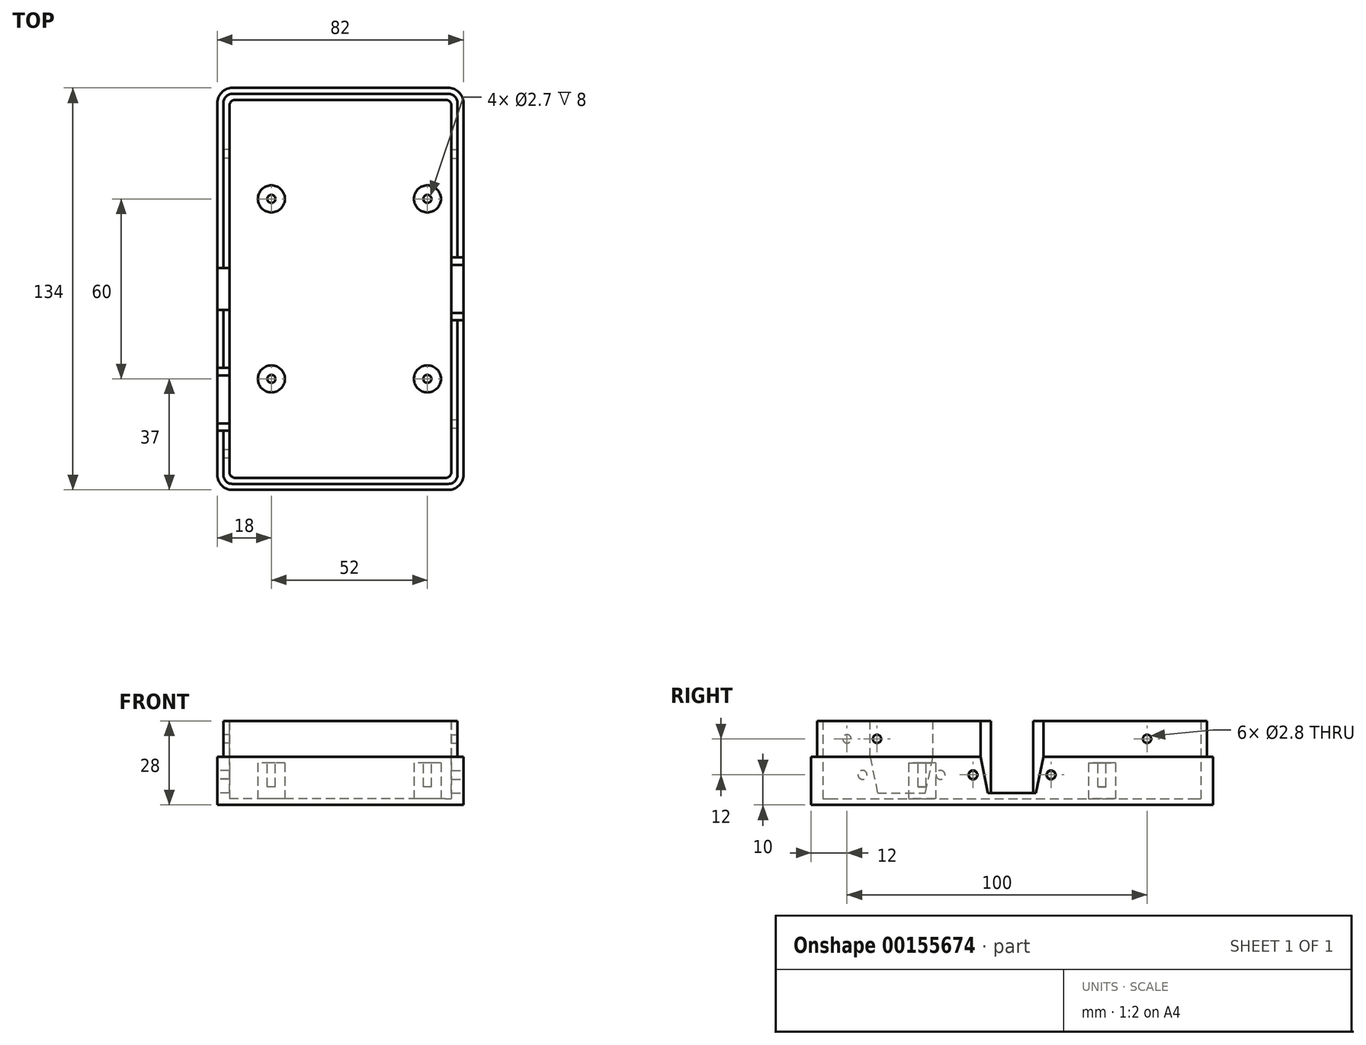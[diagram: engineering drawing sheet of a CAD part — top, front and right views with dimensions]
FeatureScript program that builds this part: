
annotation { "Feature Type Name" : "Feature", "Feature Type Description" : "" }
export const myFeature = defineFeature(function(context is Context, id is Id, definition is map)
    precondition{}
    {
        {
            var Q0;
            Q0=qCreatedBy(makeId("Top.planeOp"),FACE);
            var sketch = newSketch(context, id + "F0", { "sketchPlane" : qUnion([Q0])});
            skLineSegment(sketch, "E0.bottom", {"start": v(36, -67) * mm, "end": v(-36, -67) * mm});
            skLineSegment(sketch, "E0.top", {"start": v(36, 67) * mm, "end": v(-36, 67) * mm});
            skLineSegment(sketch, "E0.left", {"start": v(41, -62) * mm, "end": v(41, 62) * mm});
            skLineSegment(sketch, "E0.right", {"start": v(-41, -62) * mm, "end": v(-41, 62) * mm});
            skPoint(sketch, "E0.middle", {"position": v(0, 0) * mm});
            skPoint(sketch, "E1.visualSharp", {"position": v(-41, 67) * mm});
            skArc(sketch, "E1.filletArc", {"start": v(-36, 67) * mm, "mid": v(-39.54, 65.54) * mm, "end": v(-41, 62) * mm});
            skPoint(sketch, "E2.visualSharp", {"position": v(41, 67) * mm});
            skArc(sketch, "E2.filletArc", {"start": v(41, 62) * mm, "mid": v(39.54, 65.54) * mm, "end": v(36, 67) * mm});
            skPoint(sketch, "E3.visualSharp", {"position": v(41, -67) * mm});
            skArc(sketch, "E3.filletArc", {"start": v(36, -67) * mm, "mid": v(39.54, -65.54) * mm, "end": v(41, -62) * mm});
            skPoint(sketch, "E4.visualSharp", {"position": v(-41, -67) * mm});
            skArc(sketch, "E4.filletArc", {"start": v(-41, -62) * mm, "mid": v(-39.54, -65.54) * mm, "end": v(-36, -67) * mm});
            skSolve(sketch);
        }
        {
            var Q0;
            Q0=qSketchRegion(id+"F0",true);
            extrude(context, id + "F1", {"entities" : qUnion([Q0]), "depth" : 16 * mm});
        }
        {
            var Q0;
            Q0=makeQuery(id+"F1.opExtrude","CAP_FACE",FACE,{"disambiguationData":[OSD([sQuery(id+"F0.wireOp",EDGE,"E0.bottom"),sQuery(id+"F0.wireOp",EDGE,"E0.top"),sQuery(id+"F0.wireOp",EDGE,"E0.left"),sQuery(id+"F0.wireOp",EDGE,"E0.right"),sQuery(id+"F0.wireOp",EDGE,"E1.filletArc"),sQuery(id+"F0.wireOp",EDGE,"E2.filletArc"),sQuery(id+"F0.wireOp",EDGE,"E3.filletArc"),sQuery(id+"F0.wireOp",EDGE,"E4.filletArc")])],"isStart":false});
            shell(context, id + "F2", {"entities" : qUnion([Q0]), "thickness" : 2 * mm});
        }
        {
            var Q0;
            Q0=makeQuery(id+"F2.opShell","OFFSET_FACE",FACE,{"disambiguationData":[OSD([sQuery(id+"F0.wireOp",EDGE,"E0.bottom"),sQuery(id+"F0.wireOp",EDGE,"E0.top"),sQuery(id+"F0.wireOp",EDGE,"E0.left"),sQuery(id+"F0.wireOp",EDGE,"E0.right"),sQuery(id+"F0.wireOp",EDGE,"E1.filletArc"),sQuery(id+"F0.wireOp",EDGE,"E2.filletArc"),sQuery(id+"F0.wireOp",EDGE,"E3.filletArc"),sQuery(id+"F0.wireOp",EDGE,"E4.filletArc")])]});
            var sketch = newSketch(context, id + "F3", { "sketchPlane" : qUnion([Q0])});
            skCircle(sketch, "E5", {"center": v(-23, 30) * mm, "radius": 4.5 * mm});
            skCircle(sketch, "E6", {"center": v(29, 30) * mm, "radius": 4.5 * mm});
            skCircle(sketch, "E7", {"center": v(-23, -30) * mm, "radius": 4.5 * mm});
            skCircle(sketch, "E8", {"center": v(29, -30) * mm, "radius": 4.5 * mm});
            skLineSegment(sketch, "E9.bottom", {"start": v(36, -65) * mm, "end": v(-36, -65) * mm});
            skLineSegment(sketch, "E9.left", {"start": v(39, -62) * mm, "end": v(39, 62) * mm});
            skLineSegment(sketch, "E9.right", {"start": v(-39, -62) * mm, "end": v(-39, 62) * mm});
            skPoint(sketch, "E9.middle", {"position": v(0, 0) * mm});
            skLineSegment(sketch, "E10.bottom", {"start": v(35, -63) * mm, "end": v(-35, -63) * mm});
            skLineSegment(sketch, "E10.left", {"start": v(37, -61) * mm, "end": v(37, 61) * mm});
            skLineSegment(sketch, "E10.right", {"start": v(-37, -61) * mm, "end": v(-37, 61) * mm});
            skPoint(sketch, "E11.visualSharp", {"position": v(-39, -65) * mm});
            skArc(sketch, "E11.filletArc", {"start": v(-39, -62) * mm, "mid": v(-38.12, -64.12) * mm, "end": v(-36, -65) * mm});
            skPoint(sketch, "E12.visualSharp", {"position": v(39, -65) * mm});
            skArc(sketch, "E12.filletArc", {"start": v(36, -65) * mm, "mid": v(38.12, -64.12) * mm, "end": v(39, -62) * mm});
            skPoint(sketch, "E13.visualSharp", {"position": v(-39, 65) * mm});
            skArc(sketch, "E13.filletArc", {"start": v(-36, 65) * mm, "mid": v(-38.12, 64.12) * mm, "end": v(-39, 62) * mm});
            skPoint(sketch, "E14.visualSharp", {"position": v(39, 65) * mm});
            skArc(sketch, "E14.filletArc", {"start": v(39, 62) * mm, "mid": v(38.12, 64.12) * mm, "end": v(36, 65) * mm});
            skPoint(sketch, "E15.visualSharp", {"position": v(-37, 63) * mm});
            skArc(sketch, "E15.filletArc", {"start": v(-35, 63) * mm, "mid": v(-36.41, 62.41) * mm, "end": v(-37, 61) * mm});
            skPoint(sketch, "E16.visualSharp", {"position": v(37, 63) * mm});
            skArc(sketch, "E16.filletArc", {"start": v(37, 61) * mm, "mid": v(36.41, 62.41) * mm, "end": v(35, 63) * mm});
            skPoint(sketch, "E17.visualSharp", {"position": v(-37, -63) * mm});
            skArc(sketch, "E17.filletArc", {"start": v(-37, -61) * mm, "mid": v(-36.41, -62.41) * mm, "end": v(-35, -63) * mm});
            skPoint(sketch, "E18.visualSharp", {"position": v(37, -63) * mm});
            skArc(sketch, "E18.filletArc", {"start": v(35, -63) * mm, "mid": v(36.41, -62.41) * mm, "end": v(37, -61) * mm});
            skLineSegment(sketch, "E19.trimOffspring", {"start": v(36, 65) * mm, "end": v(-36, 65) * mm});
            skLineSegment(sketch, "E20.trimOffspring", {"start": v(35, 63) * mm, "end": v(-35, 63) * mm});
            skSolve(sketch);
        }
        {
            var Q0;
            Q0=makeQuery(id+"F3.imprint","IMPRINT",FACE,{"disambiguationData":[TD([[makeQuery(id+"F3.imprint","IMPRINT",EDGE,{"derivedFrom":sQuery(id+"F3.wireOp",EDGE,"E5")}),1.0]])]});
            var Q1;
            Q1=makeQuery(id+"F3.imprint","IMPRINT",FACE,{"disambiguationData":[TD([[makeQuery(id+"F3.imprint","IMPRINT",EDGE,{"derivedFrom":sQuery(id+"F3.wireOp",EDGE,"E7")}),1.0]])]});
            var Q2;
            Q2=makeQuery(id+"F3.imprint","IMPRINT",FACE,{"disambiguationData":[TD([[makeQuery(id+"F3.imprint","IMPRINT",EDGE,{"derivedFrom":sQuery(id+"F3.wireOp",EDGE,"E8")}),1.0]])]});
            var Q3;
            Q3=makeQuery(id+"F3.imprint","IMPRINT",FACE,{"disambiguationData":[TD([[makeQuery(id+"F3.imprint","IMPRINT",EDGE,{"derivedFrom":sQuery(id+"F3.wireOp",EDGE,"E6")}),1.0]])]});
            extrude(context, id + "F4", {"entities" : qUnion([Q0, Q1, Q2, Q3]), "operationType" : NewBodyOperationType.ADD, "depth" : 12 * mm});
        }
        {
            var Q0;
            Q0=makeQuery(id+"F4.opExtrude","CAP_FACE",FACE,{"disambiguationData":[OSD([sQuery(id+"F3.wireOp",EDGE,"E5")])],"isStart":false});
            var Q1;
            Q1=makeQuery(id+"F4.opExtrude","CAP_FACE",FACE,{"disambiguationData":[OSD([sQuery(id+"F3.wireOp",EDGE,"E6")])],"isStart":false});
            cPlane(context, id + "F5", {"entities" : qUnion([Q0, Q1]), "cplaneType" : CPlaneType.MID_PLANE, "offset" : 25 * mm, "width" : 150 * mm, "height" : 150 * mm});
        }
        {
            var Q0;
            Q0=qCreatedBy(id+"F5.planeOp",FACE);
            var sketch = newSketch(context, id + "F6", { "sketchPlane" : qUnion([Q0])});
            skCircle(sketch, "E21", {"center": v(-23, 30) * mm, "radius": 1.35 * mm});
            skCircle(sketch, "E22", {"center": v(29, 30) * mm, "radius": 1.35 * mm});
            skCircle(sketch, "E23", {"center": v(-23, -30) * mm, "radius": 1.35 * mm});
            skCircle(sketch, "E24", {"center": v(29, -30) * mm, "radius": 1.35 * mm});
            skSolve(sketch);
        }
        {
            var Q0;
            Q0=qSketchRegion(id+"F6",true);
            extrude(context, id + "F7", {"entities" : qUnion([Q0]), "operationType" : NewBodyOperationType.REMOVE, "oppositeDirection" : true, "depth" : 8 * mm});
        }
        {
            var Q0;
            Q0=makeQuery(id+"F3.imprint","IMPRINT",FACE,{"disambiguationData":[TD([[makeQuery(id+"F3.imprint","IMPRINT",EDGE,{"derivedFrom":sQuery(id+"F3.wireOp",EDGE,"E9.bottom")}),-1.0]])]});
            var Q1;
            Q1=makeQuery(id+"F3.imprint","IMPRINT",FACE,{"disambiguationData":[TD([[makeQuery(id+"F3.imprint","IMPRINT",EDGE,{"derivedFrom":sQuery(id+"F3.wireOp",EDGE,"E9.right")}),-1.0]])]});
            extrude(context, id + "F8", {"entities" : qUnion([Q0, Q1]), "operationType" : NewBodyOperationType.ADD, "depth" : 26 * mm});
        }
        {
            var Q0;
            Q0=makeQuery(id+"F1.opExtrude","SWEPT_FACE",FACE,{"disambiguationData":[OSD([sQuery(id+"F0.wireOp",EDGE,"E0.right")])]});
            var sketch = newSketch(context, id + "F9", { "sketchPlane" : qUnion([Q0])});
            skCircle(sketch, "E25", {"center": v(-13, 10) * mm, "radius": 1.4 * mm});
            skCircle(sketch, "E26", {"center": v(13, 10) * mm, "radius": 1.4 * mm});
            skLineSegment(sketch, "E27.bottom", {"start": v(7, 4) * mm, "end": v(-7, 4) * mm});
            skLineSegment(sketch, "E27.top", {"start": v(7, 16) * mm, "end": v(-7, 16) * mm});
            skLineSegment(sketch, "E27.left", {"start": v(7, 4) * mm, "end": v(7, 16) * mm});
            skLineSegment(sketch, "E27.right", {"start": v(-7, 4) * mm, "end": v(-7, 16) * mm});
            skPoint(sketch, "E27.middle", {"position": v(0, 10) * mm});
            skCircle(sketch, "E28", {"center": v(23.83, 10) * mm, "radius": 1.5 * mm});
            skCircle(sketch, "E29", {"center": v(49.83, 10) * mm, "radius": 1.5 * mm});
            skLineSegment(sketch, "E30", {"start": v(26.33, 16) * mm, "end": v(47.33, 16) * mm});
            skLineSegment(sketch, "E31", {"start": v(47.33, 16) * mm, "end": v(44.83, 4) * mm});
            skLineSegment(sketch, "E32", {"start": v(44.83, 4) * mm, "end": v(28.83, 4) * mm});
            skLineSegment(sketch, "E33", {"start": v(28.83, 4) * mm, "end": v(26.33, 16) * mm});
            skLineSegment(sketch, "E34.bottom", {"start": v(-7, 16) * mm, "end": v(7, 16) * mm});
            skLineSegment(sketch, "E34.top", {"start": v(-7, 28) * mm, "end": v(7, 28) * mm});
            skLineSegment(sketch, "E34.left", {"start": v(-7, 16) * mm, "end": v(-7, 28) * mm});
            skLineSegment(sketch, "E34.right", {"start": v(7, 16) * mm, "end": v(7, 28) * mm});
            skLineSegment(sketch, "E35.top", {"start": v(26.33, 28) * mm, "end": v(47.33, 28) * mm});
            skLineSegment(sketch, "E35.left", {"start": v(26.33, 16) * mm, "end": v(26.33, 28) * mm});
            skLineSegment(sketch, "E35.right", {"start": v(47.33, 16) * mm, "end": v(47.33, 28) * mm});
            skCircle(sketch, "E36", {"center": v(-45, 22) * mm, "radius": 1.4 * mm});
            skCircle(sketch, "E37", {"center": v(55, 22) * mm, "radius": 1.4 * mm});
            skSolve(sketch);
        }
        {
            var Q0;
            Q0=makeQuery(id+"F1.opExtrude","SWEPT_FACE",FACE,{"disambiguationData":[OSD([sQuery(id+"F0.wireOp",EDGE,"E0.left")])]});
            var sketch = newSketch(context, id + "F10", { "sketchPlane" : qUnion([Q0])});
            skCircle(sketch, "E38", {"center": v(-13, 10) * mm, "radius": 1.5 * mm});
            skCircle(sketch, "E39", {"center": v(13, 10) * mm, "radius": 1.5 * mm});
            skLineSegment(sketch, "E40", {"start": v(-10.5, 16) * mm, "end": v(10.5, 16) * mm});
            skLineSegment(sketch, "E41", {"start": v(10.5, 16) * mm, "end": v(8, 4) * mm});
            skLineSegment(sketch, "E42", {"start": v(8, 4) * mm, "end": v(-8, 4) * mm});
            skLineSegment(sketch, "E43", {"start": v(-8, 4) * mm, "end": v(-10.5, 16) * mm});
            skLineSegment(sketch, "E44.top", {"start": v(-10.5, 28) * mm, "end": v(10.5, 28) * mm});
            skLineSegment(sketch, "E44.left", {"start": v(-10.5, 16) * mm, "end": v(-10.5, 28) * mm});
            skLineSegment(sketch, "E44.right", {"start": v(10.5, 16) * mm, "end": v(10.5, 28) * mm});
            skCircle(sketch, "E45", {"center": v(45, 22) * mm, "radius": 1.4 * mm});
            skCircle(sketch, "E46", {"center": v(-45, 22) * mm, "radius": 1.4 * mm});
            skSolve(sketch);
        }
        {
            var Q0;
            Q0=qSketchRegion(id+"F9",true);
            extrude(context, id + "F11", {"entities" : qUnion([Q0]), "operationType" : NewBodyOperationType.REMOVE, "oppositeDirection" : true, "depth" : 4 * mm});
        }
        {
            var Q0;
            Q0=qSketchRegion(id+"F10",true);
            extrude(context, id + "F12", {"entities" : qUnion([Q0]), "operationType" : NewBodyOperationType.REMOVE, "oppositeDirection" : true, "depth" : 4 * mm});
        }
    });
